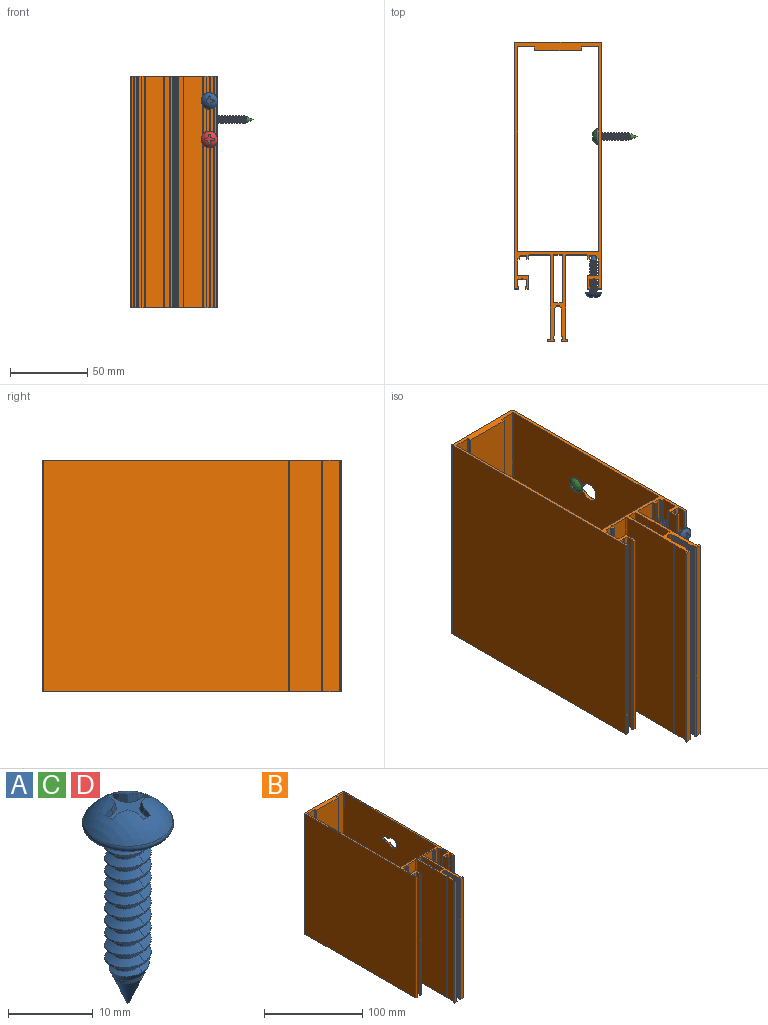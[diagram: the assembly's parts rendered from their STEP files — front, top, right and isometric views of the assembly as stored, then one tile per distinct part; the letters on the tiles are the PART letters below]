
ASSEMBLY  parts=4 mates=1
PART A: 54 faces, bbox 12.2x12.2x29.7 mm
  f0: cone r=3.6mm half-angle=25deg, axis (0,0,1), area 0.5mm2, adj f3,f38,f39,f50
  f1: cone r=2.74mm half-angle=22.5deg, axis (0,0,1), area 38.5mm2, adj f2,f6,f7,f8,f9,f10,f11,f33
  f2: cone r=2.74mm half-angle=22.5deg, axis (0,0,1), area 2mm2, adj f1,f5,f7,f8
  f3: sphere r=6.32mm, area 96.3mm2, adj f0,f4,f34,f35,f36,f37,f38,f40
  f4: torus R=4.78mm, axis (0,0,-1), area 43.7mm2, adj f3,f12
  f5: cylinder r=2.74mm len=19.08mm, axis (0,0,-1), area 41.1mm2, adj f2,f7,f8,f12,f13,f14,f15,f16
  f6: cylinder r=1.77mm len=21.44mm, axis (0,0,-1), area 59.5mm2, adj f1,f7,f8,f9,f10,f11,f12,f13
  f7: bspline ~5.48x5.48mm, area 12.7mm2, adj f1,f2,f5,f6,f9,f32
  f8: bspline ~5.48x5.48mm, area 14.7mm2, adj f1,f2,f5,f6,f10,f31
  f9: bspline ~3.81x2.15mm, area 1mm2, adj f1,f6,f7
  f10: bspline ~4.9x4.9mm, area 5.6mm2, adj f1,f6,f8,f11
  f11: bspline ~1.67x0.84mm, area 0.1mm2, adj f1,f6,f10
  f12: plane 10.03x10.03mm, normal (0,0,-1), area 56.1mm2, adj f4,f5,f6,f15,f16
  f13: bspline ~5.49x5.47mm, area 24.1mm2, adj f5,f6,f16,f18
  f14: bspline ~5.49x5.47mm, area 24.1mm2, adj f5,f6,f15,f17
  f15: bspline ~5.48x5.48mm, area 13.4mm2, adj f5,f6,f12,f14
  f16: bspline ~5.49x5.1mm, area 6.7mm2, adj f5,f6,f12,f13
  f17: bspline ~5.48x5.48mm, area 16.1mm2, adj f5,f6,f14,f20
  f18: bspline ~5.48x5.48mm, area 16.1mm2, adj f5,f6,f13,f19
  f19: bspline ~5.48x5.48mm, area 16.1mm2, adj f5,f6,f18,f22
  f20: bspline ~5.48x5.48mm, area 16.1mm2, adj f5,f6,f17,f21
  f21: bspline ~5.48x5.48mm, area 16.1mm2, adj f5,f6,f20,f24
  f22: bspline ~5.48x5.48mm, area 16.1mm2, adj f5,f6,f19,f23
  f23: bspline ~5.48x5.48mm, area 16.1mm2, adj f5,f6,f22,f26
  f24: bspline ~5.48x5.48mm, area 16.1mm2, adj f5,f6,f21,f25
  f25: bspline ~5.48x5.48mm, area 16.1mm2, adj f5,f6,f24,f28
  f26: bspline ~5.48x5.48mm, area 16.1mm2, adj f5,f6,f23,f27
  f27: bspline ~5.48x5.48mm, area 16.1mm2, adj f5,f6,f26,f30
  f28: bspline ~5.48x5.48mm, area 16.1mm2, adj f5,f6,f25,f29
  f29: bspline ~5.48x5.48mm, area 16.1mm2, adj f5,f6,f28,f32
  f30: bspline ~5.48x5.48mm, area 16.1mm2, adj f5,f6,f27,f31
  f31: bspline ~5.48x5.48mm, area 16.1mm2, adj f5,f6,f8,f30
  f32: bspline ~5.48x5.48mm, area 16.1mm2, adj f5,f6,f7,f29
  f33: plane 0.25x0.25mm, normal (0,0,-1), area 0.1mm2, adj f1
  f34: cone r=3.6mm half-angle=25deg, axis (0,0,1), area 0.5mm2, adj f3,f35,f39,f44
  f35: plane 1.07x0.89mm, normal (-0.98,0,0.17), area 0.7mm2, adj f3,f34,f36,f39
  f36: plane 1.16x1.09mm, normal (-0.91,-0.38,0.17), area 1.2mm2, adj f3,f35,f37,f39
  f37: plane 1.16x1.09mm, normal (-0.38,-0.91,0.17), area 1.2mm2, adj f3,f36,f38,f39
  f38: plane 1.07x0.89mm, normal (0,-0.98,0.17), area 0.7mm2, adj f0,f3,f37,f39
  f39: plane 6x6mm, normal (0,0,1), area 13.8mm2, adj f0,f34,f35,f36,f37,f38,f40,f41
  f40: cone r=3.6mm half-angle=25deg, axis (0,0,1), area 0.5mm2, adj f3,f39,f41,f49
  f41: plane 1.07x0.89mm, normal (0,-0.98,0.17), area 0.7mm2, adj f3,f39,f40,f42
  f42: plane 1.16x1.09mm, normal (0.38,-0.91,0.17), area 1.2mm2, adj f3,f39,f41,f43
  f43: plane 1.16x1.09mm, normal (0.91,-0.38,0.17), area 1.2mm2, adj f3,f39,f42,f44
  f44: plane 1.07x0.89mm, normal (0.98,0,0.17), area 0.7mm2, adj f3,f34,f39,f43
  f45: cone r=3.6mm half-angle=25deg, axis (0,0,1), area 0.5mm2, adj f3,f39,f46,f53
  f46: plane 1.07x0.89mm, normal (0.98,0,0.17), area 0.7mm2, adj f3,f39,f45,f47
  f47: plane 1.16x1.09mm, normal (0.91,0.38,0.17), area 1.2mm2, adj f3,f39,f46,f48
  f48: plane 1.16x1.09mm, normal (0.38,0.91,0.17), area 1.2mm2, adj f3,f39,f47,f49
  f49: plane 1.07x0.89mm, normal (0,0.98,0.17), area 0.7mm2, adj f3,f39,f40,f48
  f50: plane 1.07x0.89mm, normal (0,0.98,0.17), area 0.7mm2, adj f0,f3,f39,f51
  f51: plane 1.16x1.09mm, normal (-0.38,0.91,0.17), area 1.2mm2, adj f3,f39,f50,f52
  f52: plane 1.16x1.09mm, normal (-0.91,0.38,0.17), area 1.2mm2, adj f3,f39,f51,f53
  f53: plane 1.07x0.89mm, normal (-0.98,0,0.17), area 0.7mm2, adj f3,f39,f45,f52
PART B: 298 faces, bbox 56x194x150 mm
  f0: cylinder r=0.3mm len=150mm, axis (0,0,-1), area 70.7mm2, adj f1,f291,f292,f293
  f1: plane 150x10.48mm, normal (1,0,0), area 1572.1mm2, adj f0,f2,f292,f293
  f2: cylinder r=0.3mm len=150mm, axis (0,0,-1), area 47.1mm2, adj f1,f3,f292,f293
  f3: cylinder r=0.3mm len=150mm, axis (0,0,-1), area 94.2mm2, adj f2,f4,f292,f293
  f4: cylinder r=0.3mm len=150mm, axis (0,0,-1), area 47.1mm2, adj f3,f5,f292,f293
  f5: plane 150x41.98mm, normal (1,0,0), area 6297.1mm2, adj f4,f6,f292,f293
  f6: cylinder r=1mm len=150mm, axis (0,0,-1), area 235.6mm2, adj f5,f7,f292,f293
  f7: plane 150x12.7mm, normal (0,-1,0), area 1905mm2, adj f6,f8,f292,f293
  f8: cylinder r=0.3mm len=150mm, axis (0,0,-1), area 70.7mm2, adj f7,f9,f292,f293
  f9: plane 150x1.9mm, normal (-1,0,0), area 285mm2, adj f8,f10,f292,f293
  f10: cylinder r=0.3mm len=150mm, axis (0,0,-1), area 70.7mm2, adj f9,f11,f292,f293
  f11: plane 150x0.9mm, normal (0,-1,0), area 135mm2, adj f10,f12,f292,f293
  f12: cylinder r=0.3mm len=150mm, axis (0,0,-1), area 70.7mm2, adj f11,f13,f292,f293
  f13: plane 150x1.4mm, normal (1,0,0), area 210mm2, adj f12,f14,f292,f293
  f14: cylinder r=0.3mm len=150mm, axis (0,0,-1), area 70.7mm2, adj f13,f15,f292,f293
  f15: plane 150x3.6mm, normal (0,-1,0), area 540mm2, adj f14,f16,f292,f293
  f16: cylinder r=0.3mm len=150mm, axis (0,0,-1), area 70.7mm2, adj f15,f17,f292,f293
  f17: plane 150x1.4mm, normal (-1,0,0), area 210mm2, adj f16,f18,f292,f293
  f18: cylinder r=0.3mm len=150mm, axis (0,0,-1), area 70.7mm2, adj f17,f19,f292,f293
  f19: plane 150x1.1mm, normal (0,-1,0), area 165mm2, adj f18,f20,f292,f293
  f20: cylinder r=0.1mm len=150mm, axis (0,0,-1), area 23.6mm2, adj f19,f21,f292,f293
  f21: plane 150x10.2mm, normal (-1,0,0), area 1530mm2, adj f20,f22,f292,f293
  f22: cylinder r=0.5mm len=150mm, axis (0,0,-1), area 117.8mm2, adj f21,f23,f292,f293
  f23: plane 150x6.2mm, normal (0,1,0), area 930mm2, adj f22,f24,f292,f293
  f24: cylinder r=0.5mm len=150mm, axis (0,0,-1), area 117.8mm2, adj f23,f25,f292,f293
  f25: plane 150x7.9mm, normal (-1,0,0), area 1185mm2, adj f24,f26,f292,f293
  f26: cylinder r=0.3mm len=150mm, axis (0,0,-1), area 70.7mm2, adj f25,f27,f292,f293
  f27: plane 150x1.6mm, normal (0,-1,0), area 240mm2, adj f26,f28,f292,f293
  f28: cylinder r=0.5mm len=150mm, axis (0,0,-1), area 117.8mm2, adj f27,f29,f292,f293
  f29: plane 150x0.4mm, normal (1,0,0), area 60mm2, adj f28,f30,f292,f293
  f30: cylinder r=0.3mm len=150mm, axis (0,0,-1), area 70.7mm2, adj f29,f31,f292,f293
  f31: plane 150x0.3mm, normal (0,1,0), area 45mm2, adj f30,f32,f292,f293
  f32: cylinder r=0.3mm len=150mm, axis (0,0,-1), area 70.7mm2, adj f31,f33,f292,f293
  f33: plane 150x4.6mm, normal (1,0,0), area 690mm2, adj f32,f34,f292,f293
  f34: cylinder r=0.1mm len=150mm, axis (0,0,-1), area 23.6mm2, adj f33,f35,f292,f293
  f35: plane 150x2.38mm, normal (0,-1,0), area 357.1mm2, adj f34,f36,f292,f293
  f36: cylinder r=0.3mm len=150mm, axis (0,0,-1), area 47.1mm2, adj f35,f37,f292,f293
  f37: cylinder r=0.3mm len=150mm, axis (0,0,-1), area 94.2mm2, adj f36,f38,f292,f293
  f38: cylinder r=0.3mm len=150mm, axis (0,0,-1), area 47.1mm2, adj f37,f39,f292,f293
  f39: plane 150x2.38mm, normal (0,-1,0), area 357.1mm2, adj f38,f40,f292,f293
  f40: cylinder r=0.1mm len=150mm, axis (0,0,-1), area 23.6mm2, adj f39,f41,f292,f293
  f41: plane 150x4.6mm, normal (-1,0,0), area 690mm2, adj f40,f42,f292,f293
  f42: cylinder r=0.3mm len=150mm, axis (0,0,-1), area 70.7mm2, adj f41,f43,f292,f293
  f43: plane 150x0.3mm, normal (0,1,0), area 45mm2, adj f42,f44,f292,f293
  f44: cylinder r=0.3mm len=150mm, axis (0,0,-1), area 70.7mm2, adj f43,f45,f292,f293
  f45: plane 150x0.4mm, normal (-1,0,0), area 60mm2, adj f44,f46,f292,f293
  f46: cylinder r=0.5mm len=150mm, axis (0,0,-1), area 117.8mm2, adj f45,f47,f292,f293
  f47: plane 150x1.6mm, normal (0,-1,0), area 240mm2, adj f46,f48,f292,f293
  f48: cylinder r=0.3mm len=150mm, axis (0,0,-1), area 70.7mm2, adj f47,f49,f292,f293
  f49: plane 159.2x150mm, normal (1,0,0), area 23717.3mm2, adj f48,f50,f292,f293,f294,f295,f296,f297
  f50: cylinder r=0.5mm len=150mm, axis (0,0,-1), area 117.8mm2, adj f49,f51,f292,f293
  f51: plane 150x55mm, normal (0,1,0), area 8250mm2, adj f50,f52,f292,f293
  f52: cylinder r=0.5mm len=150mm, axis (0,0,-1), area 117.8mm2, adj f51,f53,f292,f293
  f53: plane 159.2x150mm, normal (-1,0,0), area 23880mm2, adj f52,f54,f292,f293
  f54: cylinder r=0.3mm len=150mm, axis (0,0,-1), area 70.7mm2, adj f53,f55,f292,f293
  f55: plane 150x1.6mm, normal (0,-1,0), area 240mm2, adj f54,f56,f292,f293
  f56: cylinder r=0.5mm len=150mm, axis (0,0,-1), area 117.8mm2, adj f55,f57,f292,f293
  f57: plane 150x0.4mm, normal (1,0,0), area 60mm2, adj f56,f58,f292,f293
  f58: cylinder r=0.3mm len=150mm, axis (0,0,-1), area 70.7mm2, adj f57,f59,f292,f293
  f59: plane 150x0.3mm, normal (0,1,0), area 45mm2, adj f58,f60,f292,f293
  f60: cylinder r=0.3mm len=150mm, axis (0,0,-1), area 70.7mm2, adj f59,f61,f292,f293
  f61: plane 150x4.6mm, normal (1,0,0), area 690mm2, adj f60,f62,f292,f293
  f62: cylinder r=0.1mm len=150mm, axis (0,0,-1), area 23.6mm2, adj f61,f63,f292,f293
  f63: plane 150x2.38mm, normal (0,-1,0), area 357.1mm2, adj f62,f64,f292,f293
  f64: cylinder r=0.3mm len=150mm, axis (0,0,-1), area 47.1mm2, adj f63,f65,f292,f293
  f65: cylinder r=0.3mm len=150mm, axis (0,0,-1), area 94.2mm2, adj f64,f66,f292,f293
  f66: cylinder r=0.3mm len=150mm, axis (0,0,-1), area 47.1mm2, adj f65,f67,f292,f293
  f67: plane 150x2.38mm, normal (0,-1,0), area 357.1mm2, adj f66,f68,f292,f293
  f68: cylinder r=0.1mm len=150mm, axis (0,0,-1), area 23.6mm2, adj f67,f69,f292,f293
  f69: plane 150x4.6mm, normal (-1,0,0), area 690mm2, adj f68,f70,f292,f293
  f70: cylinder r=0.3mm len=150mm, axis (0,0,-1), area 70.7mm2, adj f69,f71,f292,f293
  f71: plane 150x0.3mm, normal (0,1,0), area 45mm2, adj f70,f72,f292,f293
  f72: cylinder r=0.3mm len=150mm, axis (0,0,-1), area 70.7mm2, adj f71,f73,f292,f293
  f73: plane 150x0.4mm, normal (-1,0,0), area 60mm2, adj f72,f74,f292,f293
  f74: cylinder r=0.5mm len=150mm, axis (0,0,-1), area 117.8mm2, adj f73,f75,f292,f293
  f75: plane 150x1.6mm, normal (0,-1,0), area 240mm2, adj f74,f76,f292,f293
  f76: cylinder r=0.3mm len=150mm, axis (0,0,-1), area 70.7mm2, adj f75,f77,f292,f293
  f77: plane 150x7.9mm, normal (1,0,0), area 1185mm2, adj f76,f78,f292,f293
  f78: cylinder r=0.5mm len=150mm, axis (0,0,-1), area 117.8mm2, adj f77,f79,f292,f293
  f79: plane 150x6.2mm, normal (0,1,0), area 930mm2, adj f78,f80,f292,f293
  f80: cylinder r=0.5mm len=150mm, axis (0,0,-1), area 117.8mm2, adj f79,f81,f292,f293
  f81: plane 150x10.2mm, normal (1,0,0), area 1530mm2, adj f80,f82,f292,f293
  f82: cylinder r=0.1mm len=150mm, axis (0,0,-1), area 23.6mm2, adj f81,f83,f292,f293
  f83: plane 150x1.1mm, normal (0,-1,0), area 165mm2, adj f82,f84,f292,f293
  f84: cylinder r=0.3mm len=150mm, axis (0,0,-1), area 70.7mm2, adj f83,f85,f292,f293
  f85: plane 150x1.4mm, normal (1,0,0), area 210mm2, adj f84,f86,f292,f293
  f86: cylinder r=0.3mm len=150mm, axis (0,0,-1), area 70.7mm2, adj f85,f87,f292,f293
  f87: plane 150x3.6mm, normal (0,-1,0), area 540mm2, adj f86,f88,f292,f293
  f88: cylinder r=0.3mm len=150mm, axis (0,0,-1), area 70.7mm2, adj f87,f89,f292,f293
  f89: plane 150x1.4mm, normal (-1,0,0), area 210mm2, adj f88,f90,f292,f293
  f90: cylinder r=0.3mm len=150mm, axis (0,0,-1), area 70.7mm2, adj f89,f91,f292,f293
  f91: plane 150x0.9mm, normal (0,-1,0), area 135mm2, adj f90,f92,f292,f293
  f92: cylinder r=0.3mm len=150mm, axis (0,0,-1), area 70.7mm2, adj f91,f93,f292,f293
  f93: plane 150x1.9mm, normal (1,0,0), area 285mm2, adj f92,f94,f292,f293
  f94: cylinder r=0.3mm len=150mm, axis (0,0,-1), area 70.7mm2, adj f93,f95,f292,f293
  f95: plane 150x12.7mm, normal (0,-1,0), area 1905mm2, adj f94,f96,f292,f293
  f96: cylinder r=1mm len=150mm, axis (0,0,-1), area 235.6mm2, adj f95,f97,f292,f293
  f97: plane 150x41.98mm, normal (-1,0,0), area 6297.1mm2, adj f96,f98,f292,f293
  f98: cylinder r=0.3mm len=150mm, axis (0,0,-1), area 47.1mm2, adj f97,f99,f292,f293
  f99: cylinder r=0.3mm len=150mm, axis (0,0,-1), area 94.2mm2, adj f98,f100,f292,f293
  f100: cylinder r=0.3mm len=150mm, axis (0,0,-1), area 47.1mm2, adj f99,f101,f292,f293
  f101: plane 150x10.48mm, normal (-1,0,0), area 1572.1mm2, adj f100,f102,f292,f293
  f102: cylinder r=0.3mm len=150mm, axis (0,0,-1), area 70.7mm2, adj f101,f103,f292,f293
  f103: plane 150x0.9mm, normal (0,1,0), area 135mm2, adj f102,f104,f292,f293
  f104: cylinder r=0.3mm len=150mm, axis (0,0,-1), area 70.7mm2, adj f103,f105,f292,f293
  f105: plane 150x0.6mm, normal (-1,0,0), area 90mm2, adj f104,f106,f292,f293
  f106: cylinder r=0.3mm len=150mm, axis (0,0,-1), area 70.7mm2, adj f105,f107,f292,f293
  f107: plane 150x3.3mm, normal (0,-1,0), area 495mm2, adj f106,f108,f292,f293
  f108: cylinder r=0.8mm len=150mm, axis (0,0,-1), area 188.5mm2, adj f107,f109,f292,f293
  f109: plane 150x0.1mm, normal (1,0,0), area 15mm2, adj f108,f110,f292,f293
  f110: cylinder r=0.3mm len=150mm, axis (0,0,-1), area 70.7mm2, adj f109,f111,f292,f293
  f111: plane 150x0.3mm, normal (0,1,0), area 45mm2, adj f110,f112,f292,f293
  f112: cylinder r=0.3mm len=150mm, axis (0,0,-1), area 70.7mm2, adj f111,f113,f292,f293
  f113: plane 150x1.28mm, normal (1,0,0), area 191.4mm2, adj f112,f114,f292,f293
  f114: cylinder r=0.3mm len=150mm, axis (0,0,-1), area 35.3mm2, adj f113,f115,f292,f293
  f115: plane 150x0.82mm, normal (0.71,-0.71,0), area 174.9mm2, adj f114,f116,f292,f293
  f116: cylinder r=0.3mm len=150mm, axis (0,0,-1), area 35.3mm2, adj f115,f117,f292,f293
  f117: plane 150x0.3mm, normal (1,0,0), area 44.8mm2, adj f116,f118,f292,f293
  f118: cylinder r=0.3mm len=150mm, axis (0,0,-1), area 47.1mm2, adj f117,f119,f292,f293
  f119: plane 150x0.25mm, normal (0.5,0.87,0), area 43.3mm2, adj f118,f120,f292,f293
  f120: cylinder r=0.2mm len=150mm, axis (0,0,-1), area 62.8mm2, adj f119,f121,f292,f293
  f121: plane 150x0.25mm, normal (0.5,-0.87,0), area 43.3mm2, adj f120,f122,f292,f293
  f122: cylinder r=0.3mm len=150mm, axis (0,0,-1), area 47.1mm2, adj f121,f123,f292,f293
  f123: plane 150x0.65mm, normal (1,0,0), area 96.8mm2, adj f122,f124,f292,f293
  f124: cylinder r=0.3mm len=150mm, axis (0,0,-1), area 47.1mm2, adj f123,f125,f292,f293
  f125: plane 150x0.25mm, normal (0.5,0.87,0), area 43.3mm2, adj f124,f126,f292,f293
  f126: cylinder r=0.2mm len=150mm, axis (0,0,-1), area 62.8mm2, adj f125,f127,f292,f293
  f127: plane 150x0.25mm, normal (0.5,-0.87,0), area 43.3mm2, adj f126,f128,f292,f293
  f128: cylinder r=0.3mm len=150mm, axis (0,0,-1), area 47.1mm2, adj f127,f129,f292,f293
  f129: plane 150x0.65mm, normal (1,0,0), area 96.8mm2, adj f128,f130,f292,f293
  f130: cylinder r=0.3mm len=150mm, axis (0,0,-1), area 47.1mm2, adj f129,f131,f292,f293
  f131: plane 150x0.25mm, normal (0.5,0.87,0), area 43.3mm2, adj f130,f132,f292,f293
  f132: cylinder r=0.2mm len=150mm, axis (0,0,-1), area 62.8mm2, adj f131,f133,f292,f293
  f133: plane 150x0.25mm, normal (0.5,-0.87,0), area 43.3mm2, adj f132,f134,f292,f293
  f134: cylinder r=0.3mm len=150mm, axis (0,0,-1), area 47.1mm2, adj f133,f135,f292,f293
  f135: plane 150x0.65mm, normal (1,0,0), area 96.8mm2, adj f134,f136,f292,f293
  f136: cylinder r=0.3mm len=150mm, axis (0,0,-1), area 47.1mm2, adj f135,f137,f292,f293
  f137: plane 150x0.25mm, normal (0.5,0.87,0), area 43.3mm2, adj f136,f138,f292,f293
  f138: cylinder r=0.2mm len=150mm, axis (0,0,-1), area 62.8mm2, adj f137,f139,f292,f293
  f139: plane 150x0.25mm, normal (0.5,-0.87,0), area 43.3mm2, adj f138,f140,f292,f293
  f140: cylinder r=0.3mm len=150mm, axis (0,0,-1), area 47.1mm2, adj f139,f141,f292,f293
  f141: plane 150x0.65mm, normal (1,0,0), area 96.8mm2, adj f140,f142,f292,f293
  f142: cylinder r=0.3mm len=150mm, axis (0,0,-1), area 47.1mm2, adj f141,f143,f292,f293
  f143: plane 150x0.25mm, normal (0.5,0.87,0), area 43.3mm2, adj f142,f144,f292,f293
  f144: cylinder r=0.2mm len=150mm, axis (0,0,-1), area 62.8mm2, adj f143,f145,f292,f293
  f145: plane 150x0.25mm, normal (0.5,-0.87,0), area 43.3mm2, adj f144,f146,f292,f293
  f146: cylinder r=0.3mm len=150mm, axis (0,0,-1), area 47.1mm2, adj f145,f147,f292,f293
  f147: plane 150x0.65mm, normal (1,0,0), area 96.8mm2, adj f146,f148,f292,f293
  f148: cylinder r=0.3mm len=150mm, axis (0,0,-1), area 47.1mm2, adj f147,f149,f292,f293
  f149: plane 150x0.25mm, normal (0.5,0.87,0), area 43.3mm2, adj f148,f150,f292,f293
  f150: cylinder r=0.2mm len=150mm, axis (0,0,-1), area 62.8mm2, adj f149,f151,f292,f293
  f151: plane 150x0.25mm, normal (0.5,-0.87,0), area 43.3mm2, adj f150,f152,f292,f293
  f152: cylinder r=0.3mm len=150mm, axis (0,0,-1), area 47.1mm2, adj f151,f153,f292,f293
  f153: plane 150x0.65mm, normal (1,0,0), area 96.8mm2, adj f152,f154,f292,f293
  f154: cylinder r=0.3mm len=150mm, axis (0,0,-1), area 47.1mm2, adj f153,f155,f292,f293
  f155: plane 150x0.25mm, normal (0.5,0.87,0), area 43.3mm2, adj f154,f156,f292,f293
  f156: cylinder r=0.2mm len=150mm, axis (0,0,-1), area 62.8mm2, adj f155,f157,f292,f293
  f157: plane 150x0.25mm, normal (0.5,-0.87,0), area 43.3mm2, adj f156,f158,f292,f293
  f158: cylinder r=0.3mm len=150mm, axis (0,0,-1), area 47.1mm2, adj f157,f159,f292,f293
  f159: plane 150x0.65mm, normal (1,0,0), area 96.8mm2, adj f158,f160,f292,f293
  f160: cylinder r=0.3mm len=150mm, axis (0,0,-1), area 47.1mm2, adj f159,f161,f292,f293
  f161: plane 150x0.25mm, normal (0.5,0.87,0), area 43.3mm2, adj f160,f162,f292,f293
  f162: cylinder r=0.2mm len=150mm, axis (0,0,-1), area 62.8mm2, adj f161,f163,f292,f293
  f163: plane 150x0.25mm, normal (0.5,-0.87,0), area 43.3mm2, adj f162,f164,f292,f293
  f164: cylinder r=0.3mm len=150mm, axis (0,0,-1), area 47.1mm2, adj f163,f165,f292,f293
  f165: plane 150x0.65mm, normal (1,0,0), area 96.8mm2, adj f164,f166,f292,f293
  f166: cylinder r=0.3mm len=150mm, axis (0,0,-1), area 47.1mm2, adj f165,f167,f292,f293
  f167: plane 150x0.25mm, normal (0.5,0.87,0), area 43.3mm2, adj f166,f168,f292,f293
  f168: cylinder r=0.2mm len=150mm, axis (0,0,-1), area 62.8mm2, adj f167,f169,f292,f293
  f169: plane 150x0.25mm, normal (0.5,-0.87,0), area 43.3mm2, adj f168,f170,f292,f293
  f170: cylinder r=0.3mm len=150mm, axis (0,0,-1), area 47.1mm2, adj f169,f171,f292,f293
  f171: plane 150x0.65mm, normal (1,0,0), area 96.8mm2, adj f170,f172,f292,f293
  f172: cylinder r=0.3mm len=150mm, axis (0,0,-1), area 47.1mm2, adj f171,f173,f292,f293
  f173: plane 150x0.25mm, normal (0.5,0.87,0), area 43.3mm2, adj f172,f174,f292,f293
  f174: cylinder r=0.2mm len=150mm, axis (0,0,-1), area 31.4mm2, adj f173,f175,f292,f293
  f175: plane 150x0.15mm, normal (1,0,0), area 22.5mm2, adj f174,f176,f292,f293
  f176: cylinder r=0.3mm len=150mm, axis (0,0,-1), area 39.3mm2, adj f175,f177,f292,f293
  f177: plane 150x1.61mm, normal (0.64,-0.77,0), area 315.1mm2, adj f176,f178,f292,f293
  f178: cylinder r=0.3mm len=150mm, axis (0,0,-1), area 31.4mm2, adj f177,f179,f292,f293
  f179: plane 150x1.18mm, normal (0,-1,0), area 177.2mm2, adj f178,f180,f292,f293
  f180: cylinder r=0.3mm len=150mm, axis (0,0,-1), area 31.4mm2, adj f179,f181,f292,f293
  f181: plane 150x1.11mm, normal (-0.64,-0.77,0), area 217.2mm2, adj f180,f182,f292,f293
  f182: cylinder r=0.3mm len=150mm, axis (0,0,-1), area 39.3mm2, adj f181,f183,f292,f293
  f183: plane 150x0.89mm, normal (-1,0,0), area 133.8mm2, adj f182,f184,f292,f293
  f184: cylinder r=0.3mm len=150mm, axis (0,0,-1), area 47.1mm2, adj f183,f185,f292,f293
  f185: plane 150x0.25mm, normal (-0.5,-0.87,0), area 43.3mm2, adj f184,f186,f292,f293
  f186: cylinder r=0.2mm len=150mm, axis (0,0,-1), area 62.8mm2, adj f185,f187,f292,f293
  f187: plane 150x0.25mm, normal (-0.5,0.87,0), area 43.3mm2, adj f186,f188,f292,f293
  f188: cylinder r=0.3mm len=150mm, axis (0,0,-1), area 47.1mm2, adj f187,f189,f292,f293
  f189: plane 150x0.65mm, normal (-1,0,0), area 96.8mm2, adj f188,f190,f292,f293
  f190: cylinder r=0.3mm len=150mm, axis (0,0,-1), area 47.1mm2, adj f189,f191,f292,f293
  f191: plane 150x0.25mm, normal (-0.5,-0.87,0), area 43.3mm2, adj f190,f192,f292,f293
  f192: cylinder r=0.2mm len=150mm, axis (0,0,-1), area 62.8mm2, adj f191,f193,f292,f293
  f193: plane 150x0.25mm, normal (-0.5,0.87,0), area 43.3mm2, adj f192,f194,f292,f293
  f194: cylinder r=0.3mm len=150mm, axis (0,0,-1), area 47.1mm2, adj f193,f195,f292,f293
  f195: plane 150x0.65mm, normal (-1,0,0), area 96.8mm2, adj f194,f196,f292,f293
  f196: cylinder r=0.3mm len=150mm, axis (0,0,-1), area 47.1mm2, adj f195,f197,f292,f293
  f197: plane 150x0.25mm, normal (-0.5,-0.87,0), area 43.3mm2, adj f196,f198,f292,f293
  f198: cylinder r=0.2mm len=150mm, axis (0,0,-1), area 62.8mm2, adj f197,f199,f292,f293
  f199: plane 150x0.25mm, normal (-0.5,0.87,0), area 43.3mm2, adj f198,f200,f292,f293
  f200: cylinder r=0.3mm len=150mm, axis (0,0,-1), area 47.1mm2, adj f199,f201,f292,f293
  f201: plane 150x0.65mm, normal (-1,0,0), area 96.8mm2, adj f200,f202,f292,f293
  f202: cylinder r=0.3mm len=150mm, axis (0,0,-1), area 47.1mm2, adj f201,f203,f292,f293
  f203: plane 150x0.25mm, normal (-0.5,-0.87,0), area 43.3mm2, adj f202,f204,f292,f293
  f204: cylinder r=0.2mm len=150mm, axis (0,0,-1), area 62.8mm2, adj f203,f205,f292,f293
  f205: plane 150x0.25mm, normal (-0.5,0.87,0), area 43.3mm2, adj f204,f206,f292,f293
  f206: cylinder r=0.3mm len=150mm, axis (0,0,-1), area 47.1mm2, adj f205,f207,f292,f293
  f207: plane 150x0.65mm, normal (-1,0,0), area 96.8mm2, adj f206,f208,f292,f293
  f208: cylinder r=0.3mm len=150mm, axis (0,0,-1), area 47.1mm2, adj f207,f209,f292,f293
  f209: plane 150x0.25mm, normal (-0.5,-0.87,0), area 43.3mm2, adj f208,f210,f292,f293
  f210: cylinder r=0.2mm len=150mm, axis (0,0,-1), area 62.8mm2, adj f209,f211,f292,f293
  f211: plane 150x0.25mm, normal (-0.5,0.87,0), area 43.3mm2, adj f210,f212,f292,f293
  f212: cylinder r=0.3mm len=150mm, axis (0,0,-1), area 47.1mm2, adj f211,f213,f292,f293
  f213: plane 150x0.65mm, normal (-1,0,0), area 96.8mm2, adj f212,f214,f292,f293
  f214: cylinder r=0.3mm len=150mm, axis (0,0,-1), area 47.1mm2, adj f213,f215,f292,f293
  f215: plane 150x0.25mm, normal (-0.5,-0.87,0), area 43.3mm2, adj f214,f216,f292,f293
  f216: cylinder r=0.2mm len=150mm, axis (0,0,-1), area 62.8mm2, adj f215,f217,f292,f293
  f217: plane 150x0.25mm, normal (-0.5,0.87,0), area 43.3mm2, adj f216,f218,f292,f293
  f218: cylinder r=0.3mm len=150mm, axis (0,0,-1), area 47.1mm2, adj f217,f219,f292,f293
  f219: plane 150x0.65mm, normal (-1,0,0), area 96.8mm2, adj f218,f220,f292,f293
  f220: cylinder r=0.3mm len=150mm, axis (0,0,-1), area 47.1mm2, adj f219,f221,f292,f293
  f221: plane 150x0.25mm, normal (-0.5,-0.87,0), area 43.3mm2, adj f220,f222,f292,f293
  f222: cylinder r=0.2mm len=150mm, axis (0,0,-1), area 62.8mm2, adj f221,f223,f292,f293
  f223: plane 150x0.25mm, normal (-0.5,0.87,0), area 43.3mm2, adj f222,f224,f292,f293
  f224: cylinder r=0.3mm len=150mm, axis (0,0,-1), area 47.1mm2, adj f223,f225,f292,f293
  f225: plane 150x0.65mm, normal (-1,0,0), area 96.8mm2, adj f224,f226,f292,f293
  f226: cylinder r=0.3mm len=150mm, axis (0,0,-1), area 47.1mm2, adj f225,f227,f292,f293
  f227: plane 150x0.25mm, normal (-0.5,-0.87,0), area 43.3mm2, adj f226,f228,f292,f293
  f228: cylinder r=0.2mm len=150mm, axis (0,0,-1), area 62.8mm2, adj f227,f229,f292,f293
  f229: plane 150x0.25mm, normal (-0.5,0.87,0), area 43.3mm2, adj f228,f230,f292,f293
  f230: cylinder r=0.3mm len=150mm, axis (0,0,-1), area 47.1mm2, adj f229,f231,f292,f293
  f231: plane 150x0.65mm, normal (-1,0,0), area 96.8mm2, adj f230,f232,f292,f293
  f232: cylinder r=0.3mm len=150mm, axis (0,0,-1), area 47.1mm2, adj f231,f233,f292,f293
  f233: plane 150x0.25mm, normal (-0.5,-0.87,0), area 43.3mm2, adj f232,f234,f292,f293
  f234: cylinder r=0.2mm len=150mm, axis (0,0,-1), area 62.8mm2, adj f233,f235,f292,f293
  f235: plane 150x0.25mm, normal (-0.5,0.87,0), area 43.3mm2, adj f234,f236,f292,f293
  f236: cylinder r=0.3mm len=150mm, axis (0,0,-1), area 47.1mm2, adj f235,f237,f292,f293
  f237: plane 150x0.65mm, normal (-1,0,0), area 96.8mm2, adj f236,f238,f292,f293
  f238: cylinder r=0.3mm len=150mm, axis (0,0,-1), area 47.1mm2, adj f237,f239,f292,f293
  f239: plane 150x0.2mm, normal (-0.5,-0.87,0), area 34.6mm2, adj f238,f240,f292,f293
  f240: cylinder r=0.3mm len=150mm, axis (0,0,-1), area 47.1mm2, adj f239,f241,f292,f293
  f241: plane 150x0.42mm, normal (-1,0,0), area 62.7mm2, adj f240,f242,f292,f293
  f242: cylinder r=0.3mm len=150mm, axis (0,0,-1), area 35.3mm2, adj f241,f243,f292,f293
  f243: plane 150x0.32mm, normal (-0.71,-0.71,0), area 68.8mm2, adj f242,f244,f292,f293
  f244: cylinder r=0.3mm len=150mm, axis (0,0,-1), area 35.3mm2, adj f243,f245,f292,f293
  f245: plane 150x1.28mm, normal (-1,0,0), area 191.4mm2, adj f244,f246,f292,f293
  f246: cylinder r=0.3mm len=150mm, axis (0,0,-1), area 70.7mm2, adj f245,f247,f292,f293
  f247: plane 150x0.3mm, normal (0,1,0), area 45mm2, adj f246,f248,f292,f293
  f248: cylinder r=0.3mm len=150mm, axis (0,0,-1), area 70.7mm2, adj f247,f249,f292,f293
  f249: plane 150x0.1mm, normal (-1,0,0), area 15mm2, adj f248,f250,f292,f293
  f250: cylinder r=0.8mm len=150mm, axis (0,0,-1), area 188.5mm2, adj f249,f251,f292,f293
  f251: plane 150x3.3mm, normal (0,-1,0), area 495mm2, adj f250,f252,f292,f293
  f252: cylinder r=0.3mm len=150mm, axis (0,0,-1), area 70.7mm2, adj f251,f253,f292,f293
  f253: plane 150x0.6mm, normal (1,0,0), area 90mm2, adj f252,f254,f292,f293
  f254: cylinder r=0.3mm len=150mm, axis (0,0,-1), area 70.7mm2, adj f253,f291,f292,f293
  f255: plane 150x12.32mm, normal (1,0,0), area 1847.5mm2, adj f256,f289,f292,f293
  f256: cylinder r=0.25mm len=150mm, axis (0,0,-1), area 39.3mm2, adj f255,f257,f292,f293
  f257: cylinder r=0.25mm len=150mm, axis (0,0,-1), area 78.5mm2, adj f256,f258,f292,f293
  f258: cylinder r=0.25mm len=150mm, axis (0,0,-1), area 39.3mm2, adj f257,f259,f292,f293
  f259: plane 150x1.63mm, normal (1,0,0), area 245.1mm2, adj f258,f260,f292,f293
  f260: cylinder r=0.25mm len=150mm, axis (0,0,-1), area 39.3mm2, adj f259,f261,f292,f293
  f261: cylinder r=0.25mm len=150mm, axis (0,0,-1), area 78.5mm2, adj f260,f262,f292,f293
  f262: cylinder r=0.25mm len=150mm, axis (0,0,-1), area 39.3mm2, adj f261,f263,f292,f293
  f263: plane 150x1.63mm, normal (1,0,0), area 245.1mm2, adj f262,f264,f292,f293
  f264: cylinder r=0.25mm len=150mm, axis (0,0,-1), area 39.3mm2, adj f263,f265,f292,f293
  f265: cylinder r=0.25mm len=150mm, axis (0,0,-1), area 78.5mm2, adj f264,f266,f292,f293
  f266: cylinder r=0.25mm len=150mm, axis (0,0,-1), area 39.3mm2, adj f265,f267,f292,f293
  f267: plane 150x12.32mm, normal (1,0,0), area 1847.5mm2, adj f266,f268,f292,f293
  f268: cylinder r=0.3mm len=150mm, axis (0,0,-1), area 70.7mm2, adj f267,f269,f292,f293
  f269: plane 150x5.4mm, normal (0,-1,0), area 810mm2, adj f268,f270,f292,f293
  f270: cylinder r=0.3mm len=150mm, axis (0,0,-1), area 70.7mm2, adj f269,f271,f292,f293
  f271: plane 150x30.5mm, normal (-1,0,0), area 4575mm2, adj f270,f272,f292,f293
  f272: cylinder r=0.3mm len=150mm, axis (0,0,-1), area 70.7mm2, adj f271,f273,f292,f293
  f273: plane 150x5.4mm, normal (0,1,0), area 810mm2, adj f272,f289,f292,f293
  f274: cylinder r=0.3mm len=150mm, axis (0,0,-1), area 70.7mm2, adj f275,f290,f292,f293
  f275: plane 150x51.4mm, normal (0,1,0), area 7710mm2, adj f274,f276,f292,f293
  f276: cylinder r=0.3mm len=150mm, axis (0,0,-1), area 70.7mm2, adj f275,f277,f292,f293
  f277: plane 150x132.9mm, normal (1,0,0), area 19935mm2, adj f276,f278,f292,f293
  f278: cylinder r=0.3mm len=150mm, axis (0,0,-1), area 70.7mm2, adj f277,f279,f292,f293
  f279: plane 150x9.9mm, normal (0,-1,0), area 1485mm2, adj f278,f280,f292,f293
  f280: cylinder r=0.3mm len=150mm, axis (0,0,-1), area 70.7mm2, adj f279,f281,f292,f293
  f281: plane 150x1.9mm, normal (-1,0,0), area 285mm2, adj f280,f282,f292,f293
  f282: cylinder r=0.3mm len=150mm, axis (0,0,-1), area 70.7mm2, adj f281,f283,f292,f293
  f283: plane 150x30.4mm, normal (0,-1,0), area 4560mm2, adj f282,f284,f292,f293
  f284: cylinder r=0.3mm len=150mm, axis (0,0,-1), area 70.7mm2, adj f283,f285,f292,f293
  f285: plane 150x1.9mm, normal (1,0,0), area 285mm2, adj f284,f286,f292,f293
  f286: cylinder r=0.3mm len=150mm, axis (0,0,-1), area 70.7mm2, adj f285,f287,f292,f293
  f287: plane 150x9.9mm, normal (0,-1,0), area 1485mm2, adj f286,f288,f292,f293
  f288: cylinder r=0.3mm len=150mm, axis (0,0,-1), area 70.7mm2, adj f287,f290,f292,f293
  f289: cylinder r=0.3mm len=150mm, axis (0,0,-1), area 70.7mm2, adj f255,f273,f292,f293
  f290: plane 150x132.9mm, normal (-1,0,0), area 19772.3mm2, adj f274,f288,f292,f293,f294,f295,f296,f297
  f291: plane 150x0.9mm, normal (0,1,0), area 135mm2, adj f0,f254,f292,f293
  f292: plane 194x56mm, normal (0,0,1), area 1293.4mm2, adj f0,f1,f2,f3,f4,f5,f6,f7
  f293: plane 194x56mm, normal (0,0,-1), area 1293.4mm2, adj f0,f1,f2,f3,f4,f5,f6,f7
  f294: cylinder r=3.11mm len=6.11mm, axis (1,0,0), area 17.2mm2, adj f49,f290,f295,f297
  f295: plane 6.79x2mm, normal (0,0,-1), area 13.6mm2, adj f49,f290,f294,f296
  f296: cylinder r=6mm len=12mm, axis (1,0,0), area 62.6mm2, adj f49,f290,f295,f297
  f297: plane 6.79x2mm, normal (0,0,1), area 13.6mm2, adj f49,f290,f294,f296
PART C: same geometry as A
PART D: same geometry as A
PLACE A rot(axis=(1,0,0),90deg) t=(-103.51,-73.6,91.1)mm
PLACE B t=(-126.51,-8.37,-43.04)mm
PLACE C rot(axis=(0,-1,0),90deg) t=(-100.51,27.49,78.96)mm
PLACE D rot(axis=(1,0,0),90deg) t=(-103.51,-73.6,66.1)mm
MATE cylindrical C.f1 <-> B.f294  axis (1,0,0) through (-100.51,27.49,78.96)mm
